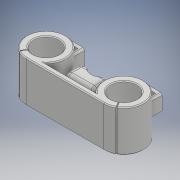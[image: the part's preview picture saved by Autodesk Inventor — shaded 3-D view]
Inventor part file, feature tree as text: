
AUTODESK INVENTOR PART (.ipt)
format: ipt  version: 2018 (Build 220112000, 112)  size: 387,072 bytes
history: native  units: mm
features: extrude x8, sketch x8, fillet x4, plane x2, chamfer x2, projected_geometry x1
ambient origin geometry x8: Origin, YZ Plane, XZ Plane, XY Plane, X Axis, Y Axis, Z Axis, Center Point
bodies: Solid1 (feature_tree)
feature tree (25):
  extrude  "Extrusion1"  Depth=45.153mm
  extrude  "Extrusion2"  Depth=24.0mm TaperAngle=0.0deg
  plane  "Work Plane3"
  extrude  "Extrusion7"  Depth=24.0mm TaperAngle=0.0deg
  plane  "Work Plane4"
  extrude  "Extrusion8"  Depth=7.0mm
  extrude  "Extrusion9"  [1 undecoded]
  extrude  "Extrusion10"  Depth=3.5mm TaperAngle=0.0deg
  chamfer  "Chamfer2"  Distance=3.5mm
  fillet  "Fillet4"  Radius=17.0mm
  fillet  "Fillet5"  Radius=15.0mm
  extrude  "Extrusion11"  Depth=2.0mm
  fillet  "Fillet6"  Radius=15.0mm
  fillet  "Fillet7"  Radius=2.0mm
  extrude  "Extrusion12"  Depth=2.0mm
  chamfer  "Chamfer3"  Distance=3.0mm
  sketch  "Sketch1"  dims[d0=15.053mm d1=45.153mm]
  sketch  "Sketch2"  dims[d2=23.0mm d3=24.0mm d4=0.0mm]
  sketch  "Sketch8"  dims[d5=3.0mm d6=24.0mm d7=0.0mm]
  sketch  "Sketch9"  dims[d33=10.0mm d34=7.0mm]
  projected_geometry  "Projected Loop1"
  sketch  "Sketch10"  dims[d35=10.0mm d36=0.0mm d37=-2.0mm]
  sketch  "Sketch11"  dims[d38=6.5mm d39=3.5mm d40=0.0mm]
  sketch  "Sketch12"  dims[d41=3.5mm d42=3.5mm d43=0.0mm d44=17.0mm d45=15.0mm]
  sketch  "Sketch13"  dims[d46=12.0mm d48=3.0mm d49=15.0mm d50=0.0mm d51=0.5mm d52=2.0mm d53=45.0deg d54=2.0mm d55=3.0mm d56=1.0mm d57=2.0mm d58=3.0mm d59=0.0mm d60=3.0mm d61=2.0mm d62=60.0deg d63=0.5mm d64=3.0mm d65=0.0mm d66=1.0mm d67=2.0mm d68=45.0deg]
note: 1 required parameter value undecoded (feature->parameter linkage not recoverable at this tier; creation-order binding heuristic only, values carry confidence <= 0.55)
